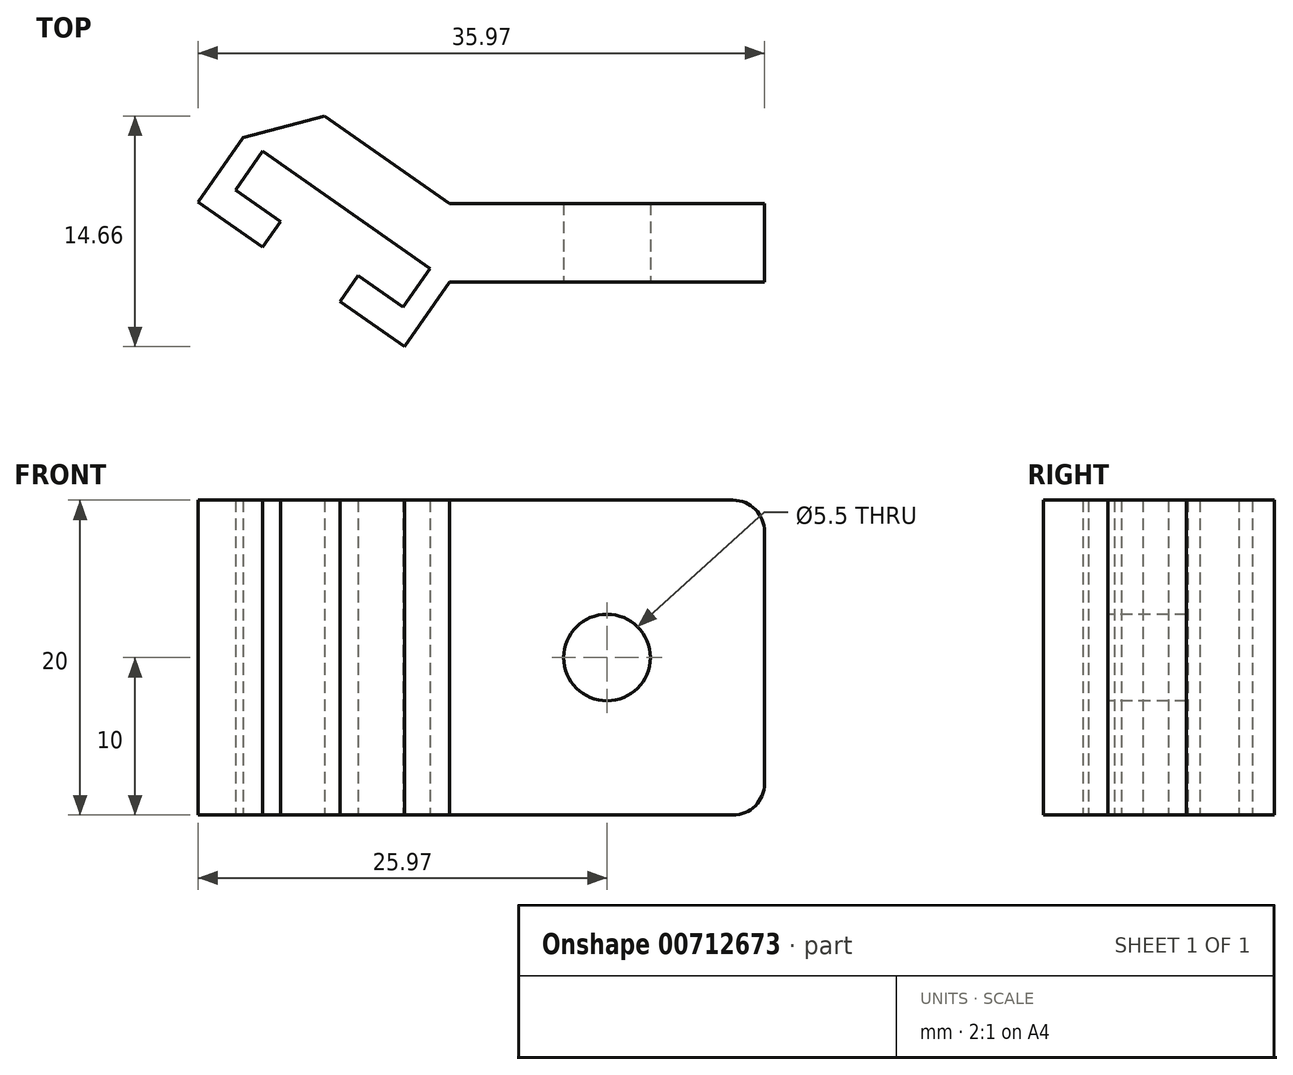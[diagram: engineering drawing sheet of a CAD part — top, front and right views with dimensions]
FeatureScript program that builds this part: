
annotation { "Feature Type Name" : "Feature", "Feature Type Description" : "" }
export const myFeature = defineFeature(function(context is Context, id is Id, definition is map)
    precondition{}
    {
        {
            var Q0;
            Q0=qCreatedBy(makeId("Top.planeOp"),FACE);
            var sketch = newSketch(context, id + "F0", { "sketchPlane" : qUnion([Q0])});
            skLineSegment(sketch, "E0.bottom", {"start": v(-10, 2.5) * mm, "end": v(10, 2.5) * mm});
            skLineSegment(sketch, "E0.top", {"start": v(-10, -2.5) * mm, "end": v(10, -2.5) * mm});
            skLineSegment(sketch, "E0.left", {"start": v(-10, 2.5) * mm, "end": v(-10, -2.5) * mm});
            skLineSegment(sketch, "E0.right", {"start": v(10, 2.5) * mm, "end": v(10, -2.5) * mm});
            skPoint(sketch, "E0.middle", {"position": v(0, 0) * mm});
            skLineSegment(sketch, "E1", {"start": v(-10, 2.5) * mm, "end": v(-17.94, 8.06) * mm});
            skLineSegment(sketch, "E2", {"start": v(-23.1, 6.68) * mm, "end": v(-17.94, 8.06) * mm});
            skLineSegment(sketch, "E3", {"start": v(-10, -2.5) * mm, "end": v(-23.1, 6.68) * mm});
            skLineSegment(sketch, "E4", {"start": v(-23.1, 6.68) * mm, "end": v(-25.97, 2.58) * mm});
            skLineSegment(sketch, "E5", {"start": v(-25.97, 2.58) * mm, "end": v(-21.88, -0.29) * mm});
            skLineSegment(sketch, "E6", {"start": v(-21.88, -0.29) * mm, "end": v(-20.73, 1.35) * mm});
            skLineSegment(sketch, "E7", {"start": v(-20.73, 1.35) * mm, "end": v(-23.6, 3.36) * mm});
            skLineSegment(sketch, "E8", {"start": v(-23.6, 3.36) * mm, "end": v(-21.88, 5.82) * mm});
            skLineSegment(sketch, "E9", {"start": v(-10, -2.5) * mm, "end": v(-12.87, -6.6) * mm});
            skLineSegment(sketch, "E10", {"start": v(-12.87, -6.6) * mm, "end": v(-16.96, -3.73) * mm});
            skLineSegment(sketch, "E11", {"start": v(-16.96, -3.73) * mm, "end": v(-15.82, -2.09) * mm});
            skLineSegment(sketch, "E12", {"start": v(-11.23, -1.64) * mm, "end": v(-12.95, -4.1) * mm});
            skLineSegment(sketch, "E13", {"start": v(-12.95, -4.1) * mm, "end": v(-15.82, -2.09) * mm});
            skSolve(sketch);
        }
        {
            var Q0;
            {var subQ3=sQuery(id+"F0.wireOp",EDGE,"E0.left");Q0=makeQuery(id+"F0.imprint","IMPRINT",FACE,{"disambiguationData":[TD([[makeQuery(id+"F0.imprint","IMPRINT",EDGE,{"derivedFrom":subQ3}),-1.0]])]});}
            var Q1;
            {var subQ0=sQuery(id+"F0.wireOp",EDGE,"hdyZA7mS-teHV-lWYu-fm4k-1SAGFMASvOwJ");Q1=makeQuery(id+"F0.imprint","IMPRINT",FACE,{"disambiguationData":[TD([[makeQuery(id+"F0.imprint","IMPRINT",EDGE,{"derivedFrom":subQ0}),1.0]])]});}
            var Q2;
            {var subQ0=sQuery(id+"F0.wireOp",EDGE,"jNdB4Np1-2dXM-6YG6-hiSc-g9QipkqpcI0V");Q2=makeQuery(id+"F0.imprint","IMPRINT",FACE,{"disambiguationData":[TD([[makeQuery(id+"F0.imprint","IMPRINT",EDGE,{"derivedFrom":subQ0}),-1.0]])]});}
            var Q3;
            Q3=makeQuery(id+"F0.imprint","IMPRINT",FACE,{"disambiguationData":[TD([[makeQuery(id+"F0.imprint","IMPRINT",EDGE,{"derivedFrom":sQuery(id+"F0.wireOp",EDGE,"E0.bottom")}),-1.0]])]});
            var Q4;
            {var subQ0=sQuery(id+"F0.wireOp",EDGE,"E4");Q4=makeQuery(id+"F0.imprint","IMPRINT",FACE,{"disambiguationData":[TD([[makeQuery(id+"F0.imprint","IMPRINT",EDGE,{"derivedFrom":subQ0}),1.0]])]});}
            var Q5;
            {var subQ0=sQuery(id+"F0.wireOp",EDGE,"E9");Q5=makeQuery(id+"F0.imprint","IMPRINT",FACE,{"disambiguationData":[TD([[makeQuery(id+"F0.imprint","IMPRINT",EDGE,{"derivedFrom":subQ0}),-1.0]])]});}
            extrude(context, id + "F1", {"entities" : qUnion([Q0, Q1, Q2, Q3, Q4, Q5]), "depth" : 20 * mm, "offsetDistance" : 25 * mm});
        }
        {
            var Q0;
            Q0=qCreatedBy(makeId("Front.planeOp"),FACE);
            var sketch = newSketch(context, id + "F2", { "sketchPlane" : qUnion([Q0])});
            skPoint(sketch, "E14", {"position": v(0, 10) * mm});
            skCircle(sketch, "E15", {"center": v(0, 10) * mm, "radius": 2.75 * mm});
            skSolve(sketch);
        }
        {
            var Q0;
            Q0 = qSketchRegion(id + "F2", true);
            extrude(context, id + "F3", {"entities" : qUnion([Q0]), "operationType" : NewBodyOperationType.REMOVE, "oppositeDirection" : true, "depth" : 6.3 * mm, "offsetDistance" : 25 * mm});
        }
        {
            var Q0;
            Q0 = qSketchRegion(id + "F2", true);
            var Q1;
            Q1=makeQuery(id+"F3.boolean.opBoolean","COPY",FACE,{"derivedFrom":makeQuery(id+"F3.opExtrude","CAP_FACE",FACE,{"disambiguationData":[OSD([sQuery(id+"F2.wireOp",EDGE,"E15")])],"isStart":true})});
            extrude(context, id + "F4", {"entities" : qUnion([Q0, Q1]), "operationType" : NewBodyOperationType.REMOVE, "endBound" : BoundingType.THROUGH_ALL, "depth" : 25 * mm, "offsetDistance" : 25 * mm});
        }
        {
            var Q0;
            Q0=makeQuery(id+"F1.opExtrude","CAP_EDGE",EDGE,{"disambiguationData":[OSD([sQuery(id+"F0.wireOp",EDGE,"E0.right")])],"isStart":false});
            var Q1;
            Q1=makeQuery(id+"F1.opExtrude","CAP_EDGE",EDGE,{"disambiguationData":[OSD([sQuery(id+"F0.wireOp",EDGE,"E0.right")])],"isStart":true});
            fillet(context, id + "F5", {"entities" : qUnion([Q0, Q1]), "radius" : 2 * mm, "tangentPropagation" : true, "allowEdgeOverflow" : false});
        }
    });
